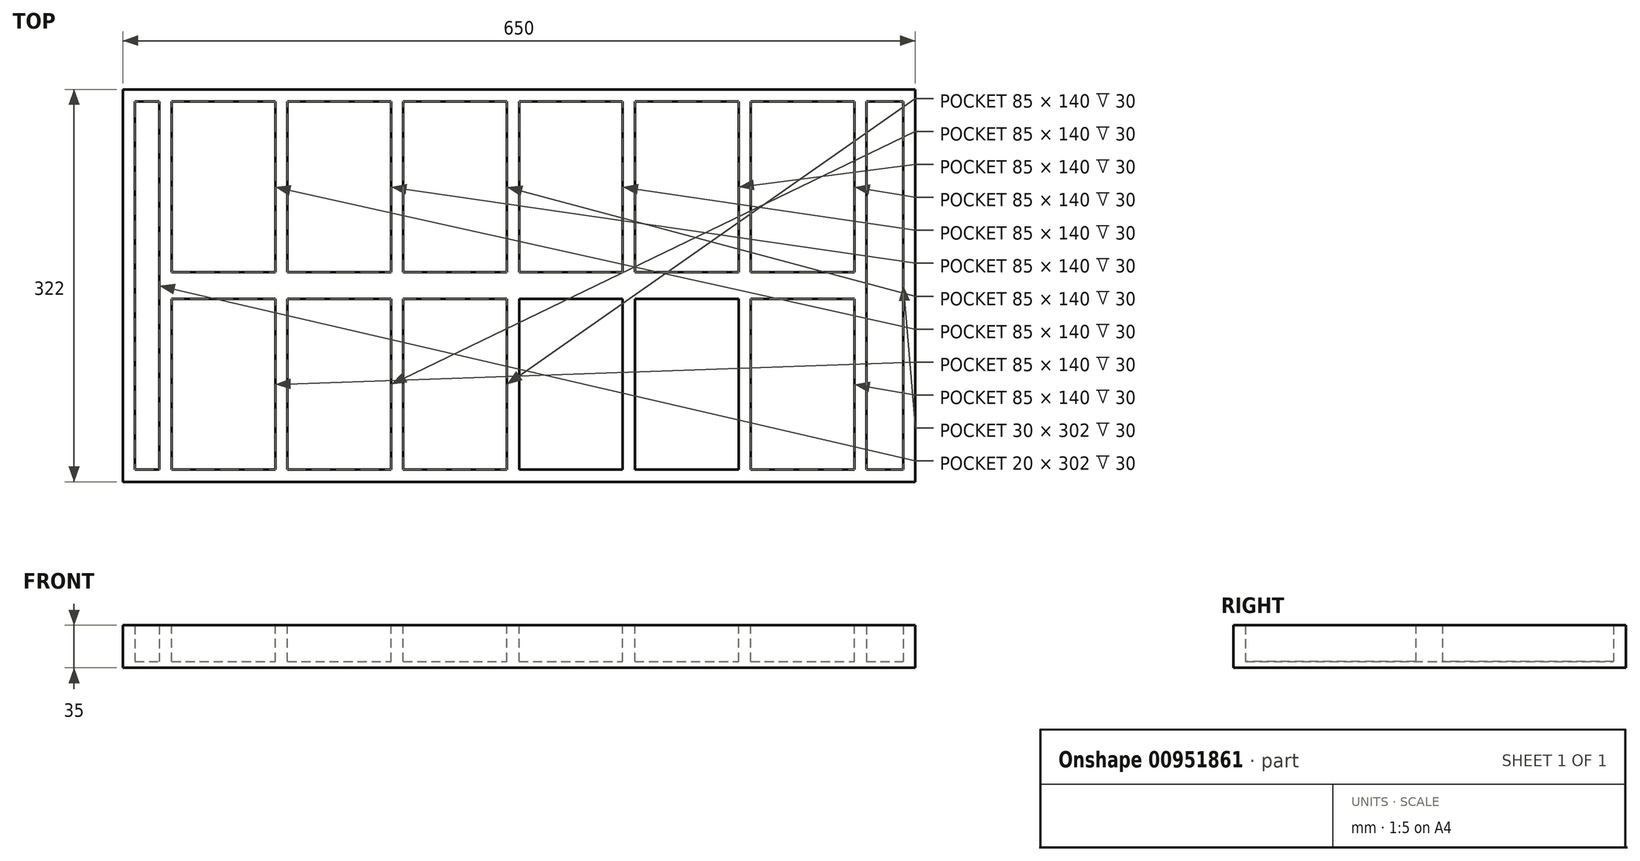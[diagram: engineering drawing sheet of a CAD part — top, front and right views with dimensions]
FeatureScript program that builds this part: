
annotation { "Feature Type Name" : "Feature", "Feature Type Description" : "" }
export const myFeature = defineFeature(function(context is Context, id is Id, definition is map)
    precondition{}
    {
        {
            var Q0;
            Q0=qCreatedBy(makeId("Top.planeOp"),FACE);
            var sketch = newSketch(context, id + "F0", { "sketchPlane" : qUnion([Q0])});
            skLineSegment(sketch, "E0.bottom", {"start": v(-290, 161) * mm, "end": v(290, 161) * mm});
            skLineSegment(sketch, "E0.top", {"start": v(-290, -161) * mm, "end": v(290, -161) * mm});
            skLineSegment(sketch, "E0.left", {"start": v(-290, 161) * mm, "end": v(-290, -161) * mm});
            skLineSegment(sketch, "E0.right", {"start": v(290, 161) * mm, "end": v(290, -161) * mm});
            skPoint(sketch, "E0.middle", {"position": v(0, 0) * mm});
            skSolve(sketch);
        }
        {
            var Q0;
            Q0=qSketchRegion(id+"F0",true);
            extrude(context, id + "F1", {"entities" : qUnion([Q0]), "depth" : 35 * mm, "offsetDistance" : 25 * mm, "symmetric" : true});
        }
        {
            var Q0;
            Q0=qCreatedBy(makeId("Top.planeOp"),FACE);
            var sketch = newSketch(context, id + "F2", { "sketchPlane" : qUnion([Q0])});
            skLineSegment(sketch, "E1.bottom", {"start": v(195, -11) * mm, "end": v(280, -11) * mm});
            skLineSegment(sketch, "E1.top", {"start": v(195, -151) * mm, "end": v(280, -151) * mm});
            skLineSegment(sketch, "E1.left", {"start": v(195, -11) * mm, "end": v(195, -151) * mm});
            skLineSegment(sketch, "E1.right", {"start": v(280, -11) * mm, "end": v(280, -151) * mm});
            skLineSegment(sketch, "E2.1.0.0", {"start": v(100, -11) * mm, "end": v(185, -11) * mm});
            skLineSegment(sketch, "E2.1.0.1", {"start": v(100, -11) * mm, "end": v(100, -151) * mm});
            skLineSegment(sketch, "E2.1.0.2", {"start": v(185, -11) * mm, "end": v(185, -151) * mm});
            skLineSegment(sketch, "E2.1.0.3", {"start": v(100, -151) * mm, "end": v(185, -151) * mm});
            skLineSegment(sketch, "E2.2.0.0", {"start": v(5, -11) * mm, "end": v(90, -11) * mm});
            skLineSegment(sketch, "E2.2.0.1", {"start": v(5, -11) * mm, "end": v(5, -151) * mm});
            skLineSegment(sketch, "E2.2.0.2", {"start": v(90, -11) * mm, "end": v(90, -151) * mm});
            skLineSegment(sketch, "E2.2.0.3", {"start": v(5, -151) * mm, "end": v(90, -151) * mm});
            skLineSegment(sketch, "E2.3.0.0", {"start": v(-90, -11) * mm, "end": v(-5, -11) * mm});
            skLineSegment(sketch, "E2.3.0.1", {"start": v(-90, -11) * mm, "end": v(-90, -151) * mm});
            skLineSegment(sketch, "E2.3.0.2", {"start": v(-5, -11) * mm, "end": v(-5, -151) * mm});
            skLineSegment(sketch, "E2.3.0.3", {"start": v(-90, -151) * mm, "end": v(-5, -151) * mm});
            skLineSegment(sketch, "E2.4.0.0", {"start": v(-185, -11) * mm, "end": v(-100, -11) * mm});
            skLineSegment(sketch, "E2.4.0.1", {"start": v(-185, -11) * mm, "end": v(-185, -151) * mm});
            skLineSegment(sketch, "E2.4.0.2", {"start": v(-100, -11) * mm, "end": v(-100, -151) * mm});
            skLineSegment(sketch, "E2.4.0.3", {"start": v(-185, -151) * mm, "end": v(-100, -151) * mm});
            skLineSegment(sketch, "E2.direction1", {"start": v(195, -151) * mm, "end": v(100, -151) * mm, "construction": true});
            skLineSegment(sketch, "E3", {"start": v(-290, 0) * mm, "end": v(290, 0) * mm, "construction": true});
            skLineSegment(sketch, "E4.MirrorCS", {"start": v(100, 151) * mm, "end": v(185, 151) * mm});
            skLineSegment(sketch, "E5.MirrorCS", {"start": v(280, 11) * mm, "end": v(280, 151) * mm});
            skLineSegment(sketch, "E6.MirrorCS", {"start": v(5, 11) * mm, "end": v(5, 151) * mm});
            skLineSegment(sketch, "E7.MirrorCS", {"start": v(-185, 11) * mm, "end": v(-100, 11) * mm});
            skLineSegment(sketch, "E8.MirrorCS", {"start": v(-185, 11) * mm, "end": v(-185, 151) * mm});
            skLineSegment(sketch, "E9.MirrorCS", {"start": v(195, 151) * mm, "end": v(280, 151) * mm});
            skLineSegment(sketch, "E10.MirrorCS", {"start": v(-100, 11) * mm, "end": v(-100, 151) * mm});
            skLineSegment(sketch, "E11.MirrorCS", {"start": v(100, 11) * mm, "end": v(185, 11) * mm});
            skLineSegment(sketch, "E12.MirrorCS", {"start": v(185, 11) * mm, "end": v(185, 151) * mm});
            skLineSegment(sketch, "E13.MirrorCS", {"start": v(195, 11) * mm, "end": v(280, 11) * mm});
            skLineSegment(sketch, "E14.MirrorCS", {"start": v(-90, 11) * mm, "end": v(-90, 151) * mm});
            skLineSegment(sketch, "E15.MirrorCS", {"start": v(90, 11) * mm, "end": v(90, 151) * mm});
            skLineSegment(sketch, "E16.MirrorCS", {"start": v(195, 151) * mm, "end": v(100, 151) * mm, "construction": true});
            skLineSegment(sketch, "E17.MirrorCS", {"start": v(100, 11) * mm, "end": v(100, 151) * mm});
            skLineSegment(sketch, "E18.MirrorCS", {"start": v(-90, 11) * mm, "end": v(-5, 11) * mm});
            skLineSegment(sketch, "E19.MirrorCS", {"start": v(-185, 151) * mm, "end": v(-100, 151) * mm});
            skLineSegment(sketch, "E20.MirrorCS", {"start": v(5, 11) * mm, "end": v(90, 11) * mm});
            skLineSegment(sketch, "E21.MirrorCS", {"start": v(-5, 11) * mm, "end": v(-5, 151) * mm});
            skLineSegment(sketch, "E22.MirrorCS", {"start": v(195, 11) * mm, "end": v(195, 151) * mm});
            skLineSegment(sketch, "E23.MirrorCS", {"start": v(-90, 151) * mm, "end": v(-5, 151) * mm});
            skLineSegment(sketch, "E24.MirrorCS", {"start": v(5, 151) * mm, "end": v(90, 151) * mm});
            skLineSegment(sketch, "E25", {"start": v(-280, 161) * mm, "end": v(-280, -161) * mm, "construction": true});
            skLineSegment(sketch, "E26.bottom", {"start": v(-280, 151) * mm, "end": v(-195, 151) * mm});
            skLineSegment(sketch, "E26.top", {"start": v(-280, 11) * mm, "end": v(-195, 11) * mm});
            skLineSegment(sketch, "E26.left", {"start": v(-280, 151) * mm, "end": v(-280, 11) * mm});
            skLineSegment(sketch, "E26.right", {"start": v(-195, 151) * mm, "end": v(-195, 11) * mm});
            skLineSegment(sketch, "E27.bottom", {"start": v(-280, -11) * mm, "end": v(-195, -11) * mm});
            skLineSegment(sketch, "E27.top", {"start": v(-280, -151) * mm, "end": v(-195, -151) * mm});
            skLineSegment(sketch, "E27.left", {"start": v(-280, -11) * mm, "end": v(-280, -151) * mm});
            skLineSegment(sketch, "E27.right", {"start": v(-195, -11) * mm, "end": v(-195, -151) * mm});
            skLineSegment(sketch, "E28", {"start": v(-185, 151) * mm, "end": v(-290, 151) * mm, "construction": true});
            skLineSegment(sketch, "E29", {"start": v(-185, -151) * mm, "end": v(-290, -151) * mm, "construction": true});
            skLineSegment(sketch, "E30", {"start": v(-195, 151) * mm, "end": v(-195, -151) * mm, "construction": true});
            skPoint(sketch, "E31", {"position": v(-280, 151) * mm});
            skPoint(sketch, "E32", {"position": v(-280, -151) * mm});
            skLineSegment(sketch, "E33", {"start": v(-290, 11) * mm, "end": v(-195, 11) * mm, "construction": true});
            skLineSegment(sketch, "E34", {"start": v(-290, -11) * mm, "end": v(-195, -11) * mm, "construction": true});
            skPoint(sketch, "E35", {"position": v(-280, -11) * mm});
            skSolve(sketch);
        }
        {
            var Q0;
            Q0=qSketchRegion(id+"F2",true);
            extrude(context, id + "F3", {"entities" : qUnion([Q0]), "operationType" : NewBodyOperationType.REMOVE, "oppositeDirection" : true, "depth" : 50 * mm, "offsetDistance" : 25 * mm, "symmetric" : true});
        }
        {
            var Q0;
            Q0=makeQuery(id+"F1.opExtrude","SWEPT_FACE",FACE,{"disambiguationData":[OSD([sQuery(id+"F0.wireOp",EDGE,"E0.left")])]});
            var sketch = newSketch(context, id + "F4", { "sketchPlane" : qUnion([Q0])});
            skLineSegment(sketch, "E36.bottom", {"start": v(-161, -17.5) * mm, "end": v(161, -17.5) * mm});
            skLineSegment(sketch, "E36.top", {"start": v(-161, 17.5) * mm, "end": v(161, 17.5) * mm});
            skLineSegment(sketch, "E36.left", {"start": v(-161, -17.5) * mm, "end": v(-161, 17.5) * mm});
            skLineSegment(sketch, "E36.right", {"start": v(161, -17.5) * mm, "end": v(161, 17.5) * mm});
            skPoint(sketch, "E36.middle", {"position": v(0, 0) * mm});
            skSolve(sketch);
        }
        {
            var Q0;
            Q0=qSketchRegion(id+"F4",true);
            extrude(context, id + "F5", {"entities" : qUnion([Q0]), "depth" : 30 * mm, "offsetDistance" : 25 * mm});
        }
        {
            var Q0;
            Q0=makeQuery(id+"F5.opExtrude","SWEPT_FACE",FACE,{"disambiguationData":[OSD([sQuery(id+"F4.wireOp",EDGE,"E36.bottom")])]});
            var sketch = newSketch(context, id + "F6", { "sketchPlane" : qUnion([Q0])});
            skLineSegment(sketch, "E37.bottom", {"start": v(-290, -151) * mm, "end": v(-310, -151) * mm});
            skLineSegment(sketch, "E37.top", {"start": v(-290, 151) * mm, "end": v(-310, 151) * mm});
            skLineSegment(sketch, "E37.left", {"start": v(-290, -151) * mm, "end": v(-290, 151) * mm});
            skLineSegment(sketch, "E37.right", {"start": v(-310, -151) * mm, "end": v(-310, 151) * mm});
            skSolve(sketch);
        }
        {
            var Q0;
            Q0=qSketchRegion(id+"F6",true);
            extrude(context, id + "F7", {"entities" : qUnion([Q0]), "operationType" : NewBodyOperationType.REMOVE, "endBound" : BoundingType.THROUGH_ALL, "oppositeDirection" : true, "depth" : 25 * mm, "offsetDistance" : 25 * mm});
        }
        {
            var Q0;
            Q0=makeQuery(id+"F1.opExtrude","SWEPT_FACE",FACE,{"disambiguationData":[OSD([sQuery(id+"F0.wireOp",EDGE,"E0.right")])]});
            var sketch = newSketch(context, id + "F8", { "sketchPlane" : qUnion([Q0])});
            skLineSegment(sketch, "E38.bottom", {"start": v(-161, 17.5) * mm, "end": v(161, 17.5) * mm});
            skLineSegment(sketch, "E38.top", {"start": v(-161, -17.5) * mm, "end": v(161, -17.5) * mm});
            skLineSegment(sketch, "E38.left", {"start": v(-161, 17.5) * mm, "end": v(-161, -17.5) * mm});
            skLineSegment(sketch, "E38.right", {"start": v(161, 17.5) * mm, "end": v(161, -17.5) * mm});
            skPoint(sketch, "E38.middle", {"position": v(0, 0) * mm});
            skSolve(sketch);
        }
        {
            var Q0;
            Q0=qSketchRegion(id+"F8",true);
            extrude(context, id + "F9", {"entities" : qUnion([Q0]), "depth" : 40 * mm, "offsetDistance" : 25 * mm});
        }
        {
            var Q0;
            Q0=makeQuery(id+"F9.opExtrude","SWEPT_FACE",FACE,{"disambiguationData":[OSD([sQuery(id+"F8.wireOp",EDGE,"E38.top")])]});
            var sketch = newSketch(context, id + "F10", { "sketchPlane" : qUnion([Q0])});
            skLineSegment(sketch, "E39", {"start": v(290, 151) * mm, "end": v(320, 151) * mm});
            skLineSegment(sketch, "E40", {"start": v(320, 151) * mm, "end": v(320, -151) * mm});
            skLineSegment(sketch, "E41", {"start": v(320, -151) * mm, "end": v(290, -151) * mm});
            skSolve(sketch);
        }
        {
            var Q0;
            Q0=qSketchRegion(id+"F10",true);
            var Q1;
            {var subQ0=sQuery(id+"F10.wireOp",EDGE,"E39");Q1=makeQuery(id+"F10.imprint","IMPRINT",FACE,{"disambiguationData":[TD([[makeQuery(id+"F10.imprint","IMPRINT",EDGE,{"derivedFrom":subQ0}),-1.0]])]});}
            extrude(context, id + "F11", {"entities" : qUnion([Q0, Q1]), "operationType" : NewBodyOperationType.REMOVE, "endBound" : BoundingType.THROUGH_ALL, "oppositeDirection" : true, "depth" : 25 * mm, "offsetDistance" : 25 * mm});
        }
        {
            var Q0;
            Q0=makeQuery(id+"F5.opExtrude","SWEPT_BODY",BODY,{"disambiguationData":[OSD([sQuery(id+"F4.wireOp",EDGE,"E36.bottom"),sQuery(id+"F4.wireOp",EDGE,"E36.top"),sQuery(id+"F4.wireOp",EDGE,"E36.left"),sQuery(id+"F4.wireOp",EDGE,"E36.right")])]});
            var Q1;
            Q1=makeQuery(id+"F1.opExtrude","SWEPT_BODY",BODY,{"disambiguationData":[OSD([sQuery(id+"F0.wireOp",EDGE,"E0.bottom"),sQuery(id+"F0.wireOp",EDGE,"E0.top"),sQuery(id+"F0.wireOp",EDGE,"E0.left"),sQuery(id+"F0.wireOp",EDGE,"E0.right")])]});
            var Q2;
            Q2=makeQuery(id+"F9.opExtrude","SWEPT_BODY",BODY,{"disambiguationData":[OSD([sQuery(id+"F8.wireOp",EDGE,"E38.bottom"),sQuery(id+"F8.wireOp",EDGE,"E38.top"),sQuery(id+"F8.wireOp",EDGE,"E38.left"),sQuery(id+"F8.wireOp",EDGE,"E38.right")])]});
            booleanBodies(context, id + "F12", {"operationType" : BooleanOperationType.UNION, "tools" : qUnion([Q0, Q1, Q2])});
        }
        {
            var Q0;
            Q0=makeQuery(id+"F12.opBoolean","MERGE",FACE,{"derivedFrom":[makeQuery(id+"F1.opExtrude","CAP_FACE",FACE,{"disambiguationData":[OSD([sQuery(id+"F0.wireOp",EDGE,"E0.bottom"),sQuery(id+"F0.wireOp",EDGE,"E0.top"),sQuery(id+"F0.wireOp",EDGE,"E0.left"),sQuery(id+"F0.wireOp",EDGE,"E0.right")])],"isStart":true}),makeQuery(id+"F5.opExtrude","SWEPT_FACE",FACE,{"disambiguationData":[OSD([sQuery(id+"F4.wireOp",EDGE,"E36.bottom")])]}),makeQuery(id+"F9.opExtrude","SWEPT_FACE",FACE,{"disambiguationData":[OSD([sQuery(id+"F8.wireOp",EDGE,"E38.top")])]})]});
            var sketch = newSketch(context, id + "F13", { "sketchPlane" : qUnion([Q0])});
            skLineSegment(sketch, "E42", {"start": v(320, 0) * mm, "end": v(-320, 0) * mm, "construction": true});
            skLineSegment(sketch, "E43", {"start": v(185, -75.62) * mm, "end": v(185, 62.33) * mm, "construction": true});
            skLineSegment(sketch, "E44", {"start": v(100, -75.62) * mm, "end": v(100, 63.74) * mm, "construction": true});
            skPoint(sketch, "E45", {"position": v(185, 0) * mm});
            skPoint(sketch, "E46", {"position": v(100, 0) * mm});
            skPoint(sketch, "E47", {"position": v(142.5, 0) * mm});
            skLineSegment(sketch, "E48", {"start": v(-90, -11) * mm, "end": v(-100, 11) * mm, "construction": true});
            skLineSegment(sketch, "E49", {"start": v(-100, -11) * mm, "end": v(-90, 11) * mm, "construction": true});
            skPoint(sketch, "E50", {"position": v(-95, 0) * mm});
            skLineSegment(sketch, "E51", {"start": v(-195, -11) * mm, "end": v(-185, 11) * mm, "construction": true});
            skPoint(sketch, "E52", {"position": v(-190, 0) * mm});
            skLineSegment(sketch, "E53", {"start": v(90, -32.12) * mm, "end": v(90, 28.55) * mm, "construction": true});
            skLineSegment(sketch, "E54", {"start": v(5, -26.43) * mm, "end": v(5, 35.5) * mm, "construction": true});
            skLineSegment(sketch, "E55", {"start": v(50, -39.7) * mm, "end": v(50, 30.45) * mm, "construction": true});
            skPoint(sketch, "E56", {"position": v(50, 0) * mm});
            skLineSegment(sketch, "E57.bottom", {"start": v(320, -151) * mm, "end": v(-310, -151) * mm});
            skLineSegment(sketch, "E57.top", {"start": v(320, 151) * mm, "end": v(-310, 151) * mm});
            skLineSegment(sketch, "E57.left", {"start": v(320, -151) * mm, "end": v(320, 151) * mm});
            skLineSegment(sketch, "E57.right", {"start": v(-310, -151) * mm, "end": v(-310, 151) * mm});
            skSolve(sketch);
        }
        {
            var Q0;
            Q0=qSketchRegion(id+"F13",true);
            extrude(context, id + "F14", {"entities" : qUnion([Q0]), "operationType" : NewBodyOperationType.ADD, "oppositeDirection" : true, "depth" : 5 * mm, "offsetDistance" : 25 * mm});
        }
    });
